# Revit family: Fire-Escape
name_source: partatom
category: Security Devices
units: mm (PartAtom-declared; Revit-internal decimal feet)

## family parameters
Always vertical = Yes
Classification Number = 23.30.70.24.11.11
Cut with Voids When Loaded = No
Host = Wall
Maintain Annotation Orientation = No
Part Type = Normal
Room Calculation Point = No
Round Connector Dimension = Use Diameter
Shared = No

## types (1)
- Fire-Escape
    Assembly Code = D4090
    Construction Details = http://www.arcat.com
    Default Elevation = 0' - 0"
    Description = Fire Escape
    Expected Lifespan (Years) = 30
    Frame Material = ARCAT - Metal - Iron, Painted, Grey
    Green Building-LEED = http://www.arcat.com
    Gross Depth = 1' - 3"
    Gross Height = 3' - 6"
    Gross Projection = 3' - 0"
    Gross Width = 6' - 0"
    Keynote = 05500
    Ladder Length = 11' - 0"
    Maintenance Schedule (Months) = 12
    Manufacturer = Generic
    Manufacturer Fax = (203) 929-2444
    Manufacturer Website = http://www.arcat.com
    Model = Generic
    Product Data = http://www.arcat.com
    Product Properties = http://www.arcat.com
    Specification = http://www.arcat.com
    Warranty Duration (Years) = 1
    flrarry = 19
    frntarry = 24
    ladarry = 10
    railarrysd = 5

## geometry (parser evidence)
native form markers: Sweep x4
no freeform markers — native parametric forms only
